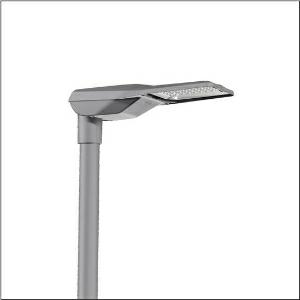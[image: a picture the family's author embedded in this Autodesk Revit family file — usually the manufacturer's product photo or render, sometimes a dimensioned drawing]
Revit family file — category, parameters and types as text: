
# Revit family: streetlight_sl_21_iq_mini___st0_5a_5xe2b31g08gb_b1a9
name_source: partatom
category: Lighting Fixtures
units: mm (PartAtom-declared; Revit-internal decimal feet)

## family parameters
Cut with Voids When Loaded = No
Host = Face
Light Source = No
Part Type = Normal
Room Calculation Point = No
Round Connector Dimension = Use Diameter
Shared = No

## types (1)
- --- (1 x LED, 5680 lm, 37.1 W, 3000K)
    Apparent Load = 37 VA
    CIE Flux Codes = 41 75 97 100 100
    Color Rendering = 70
    Color Temperature = 3000K
    Default Elevation = 1800 mm
    Description = Streetlight SL 21 iQ mini, mast luminaire, primary light control with lens, of PMMA, primary optical cover: cover, of toughened safety glass, transparent, light distribution: ST0.5a, light emission: direct distribution, primary light characteristic: asymmetric, installation type: post-top, side-entry, LED, High Power LED, rated luminous flux: 5.680lm, luminous efficacy: 153lm/W, light colour: 730, colour temperature: 3000K, control gear: iQ Street-Remote, control: Street-Remote, Auto-Match, Temp-Guard, Lumen-Switch, Night-Set, Smart-Wire, Light-Fading, Desk-Remote (wireless, voltage-free reading and setting of iQ features in the workshop via application-optimized NFC function/RFID function), optimised constant luminous flux control (CLO 2.0), pre-setting: linear dimming characteristic, mains connection: 220..240V, AC, 50/60Hz, start of lifetime: 37W, end of service life: 39W, reduction: 18W, luminaire housing, of diecast aluminium, powder-coated, SITECO metallic grey (DB 702S), corrosivity category C5 high according to DIN EN ISO 12944, please order mast flange separately, inclination adjustable: 0°, 5°, 10°, 15°, sealing non-destructively replaceable, multi-level sealing system, length: 628mm, width: 235mm, height: 110mm, mast flange for spigot size: 42mm (side-entry): 5XC10008XM4, 60/48mm (side-entry/post-top): 5XC10108XM2, 76/60mm (side-entry/post-top): 5XC10108XM1, mounting height: 4..8m, protection rating (complete): IP66, insulation class (complete): insulation class II (safety insulation), certification: CE, ENEC, ENEC+, VDE, impact resistance: IK10, permissible operating ambient temperature for outdoor applications: -40..+50°C, standard-compliant lighting for roads and squares, packaging unit: 1 piece

Light Distribution: ST0.5a
    Height = 110 mm
    Lamp = 1 x LED
    Lamp Light Flux = 5680 lm
    Lamp Power = 37.1 W
    Lamp count = 1
    Length = 625 mm
    Luminous efficacy = 153 lm/W
    Manufacturer = Siteco
    ModVariant = No
    Model = 5XE2B31G08GB
    Number of Poles = 1
    OnlyDefault = Yes
    Power Factor = 1
    Product Name = Streetlight SL 21 iQ mini | ST0.5a
    Product group = mast luminaire | pylon top
    ProductGroupID = 6100
    Protection Class = Protection class II
    Protection Degree = IP 66
    RLX_Detail_Level = 1
    RLX_Emergency_Light_Flux = 0 lm
    RLX_Emergency_Type = 0
    RLX_Emergency_Type_DB = No
    RlxData = <blob elided: 37373 chars, md5=3bba1757>
    Socket = socket
    Standby Power = 0 W
    System Light Flux = 5680 lm
    System Power = 37 W
    Type Comments = factory setting: luminous flux: 100 % | dim-lin: 254 | 385 mA
    Type Image = l_1003519.jpg
    URL = http://relux.com
    VarID = @adj_188839
    Voltage = 0 V
    Weight = 0.00 kg
    Width = 234 mm

## geometry (parser evidence)
native form markers: Blend x4, Sweep x10
no freeform markers — native parametric forms only
